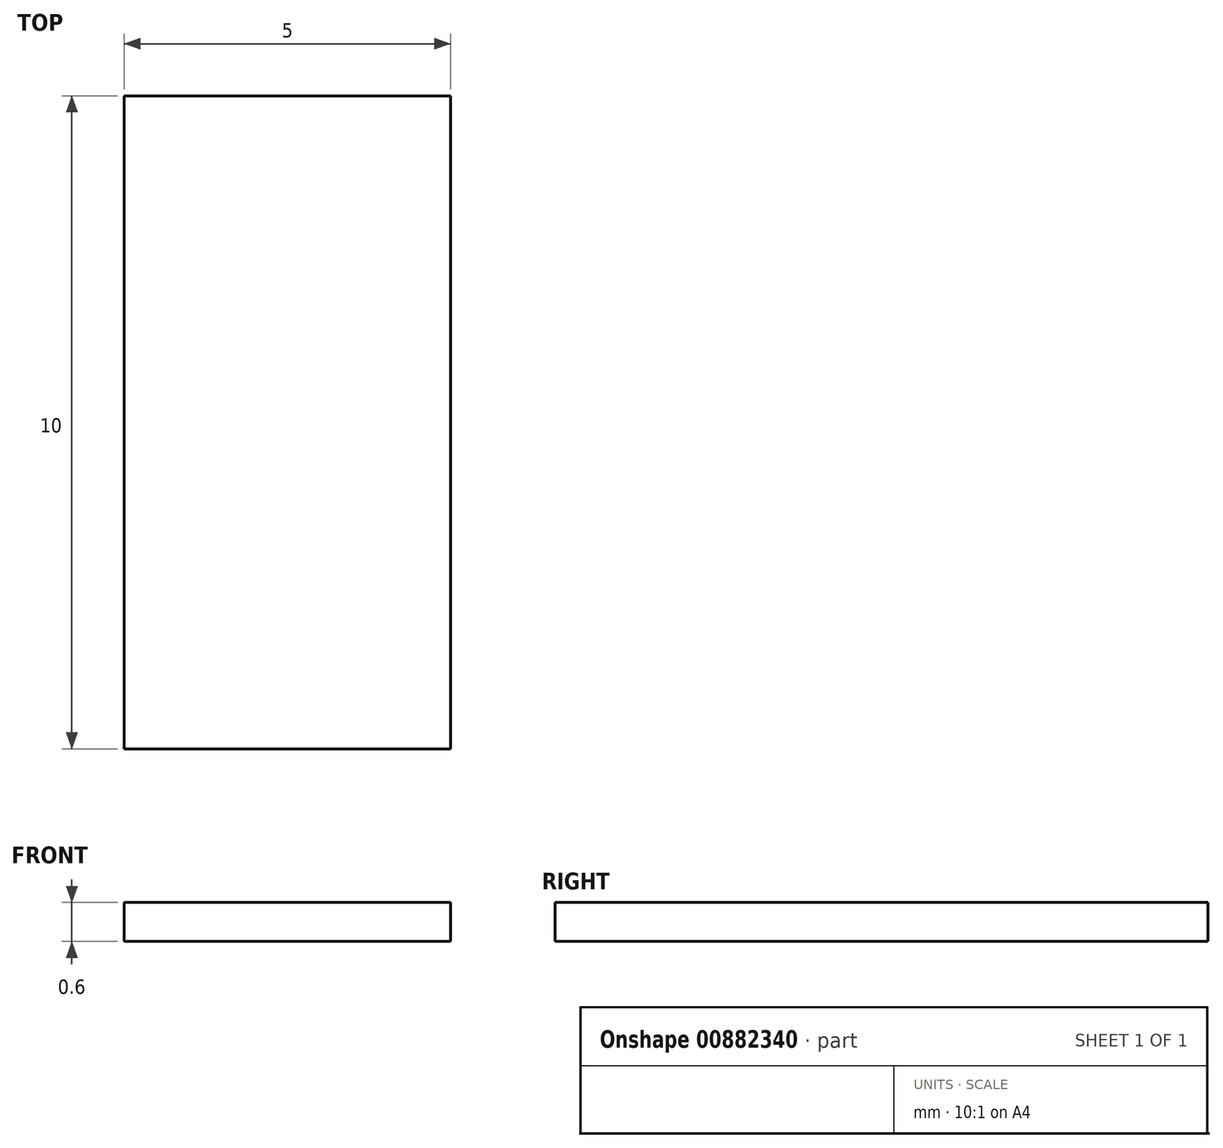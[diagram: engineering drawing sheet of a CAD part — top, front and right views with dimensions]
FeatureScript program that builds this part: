
annotation { "Feature Type Name" : "Feature", "Feature Type Description" : "" }
export const myFeature = defineFeature(function(context is Context, id is Id, definition is map)
    precondition{}
    {
        {
            var Q0;
            Q0=qCreatedBy(makeId("Top.planeOp"),FACE);
            var sketch = newSketch(context, id + "F0", { "sketchPlane" : qUnion([Q0])});
            skLineSegment(sketch, "E0.bottom", {"start": v(-1.1, 5.32) * mm, "end": v(3.9, 5.32) * mm});
            skLineSegment(sketch, "E0.top", {"start": v(-1.1, -4.68) * mm, "end": v(3.9, -4.68) * mm});
            skLineSegment(sketch, "E0.left", {"start": v(-1.1, 5.32) * mm, "end": v(-1.1, -4.68) * mm});
            skLineSegment(sketch, "E0.right", {"start": v(3.9, 5.32) * mm, "end": v(3.9, -4.68) * mm});
            skSolve(sketch);
        }
        {
            var Q0;
            Q0=makeQuery(id+"F0.imprint","IMPRINT",FACE,{"disambiguationData":[TD([[makeQuery(id+"F0.imprint","IMPRINT",EDGE,{"derivedFrom":sQuery(id+"F0.wireOp",EDGE,"E0.bottom")}),-1.0]])]});
            extrude(context, id + "F1", {"entities" : qUnion([Q0]), "depth" : 0.6 * mm, "offsetDistance" : 25 * mm});
        }
    });
